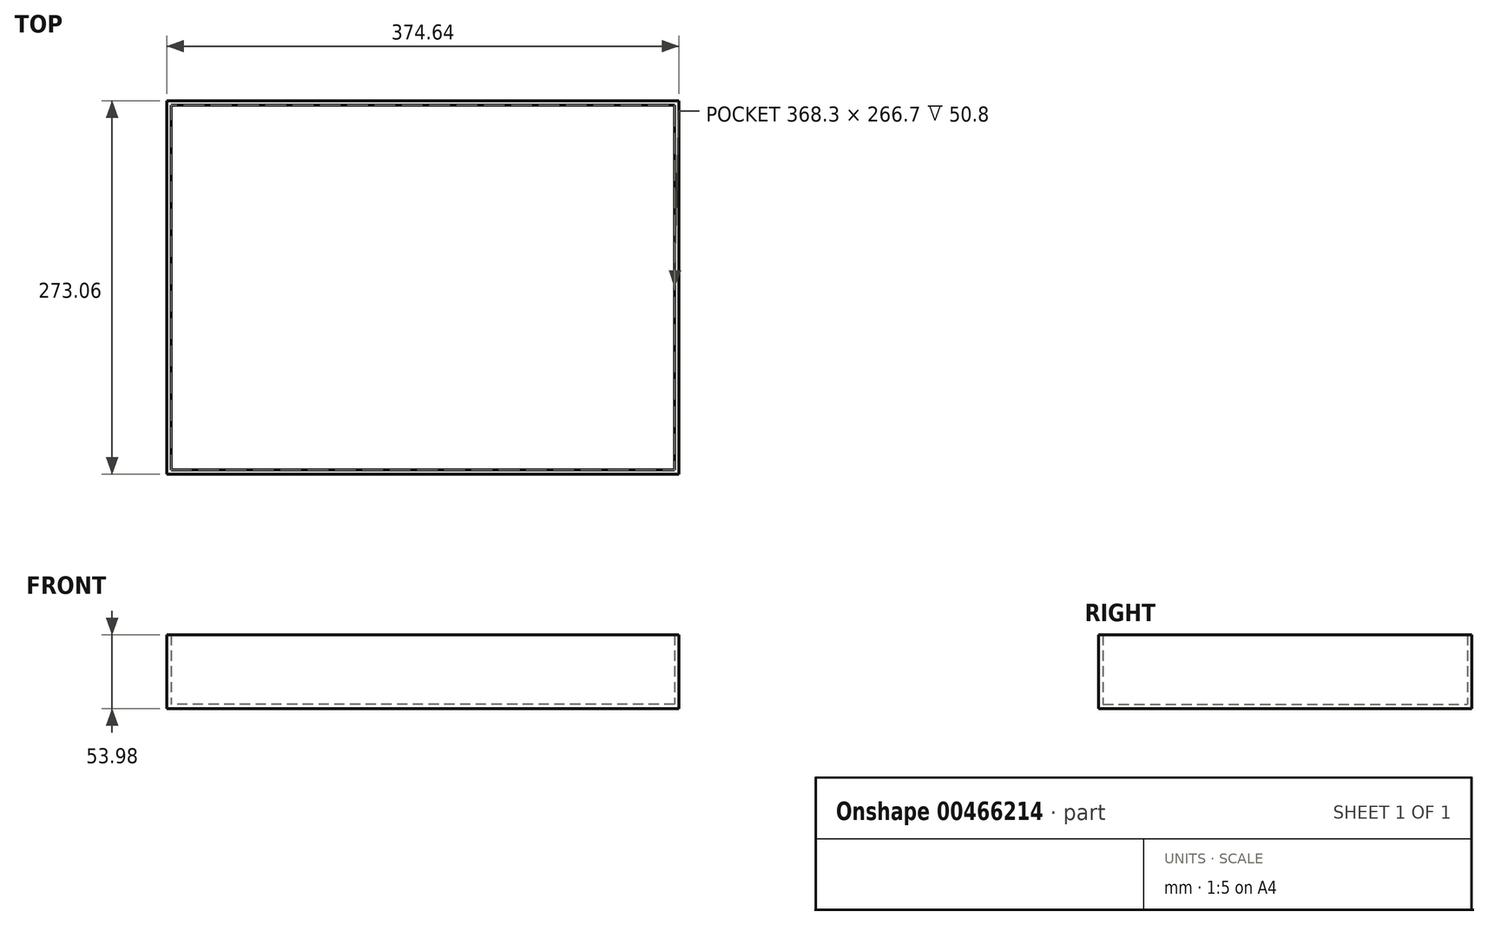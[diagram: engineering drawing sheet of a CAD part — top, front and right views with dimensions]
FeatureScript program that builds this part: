
annotation { "Feature Type Name" : "Feature", "Feature Type Description" : "" }
export const myFeature = defineFeature(function(context is Context, id is Id, definition is map)
    precondition{}
    {
        {
            var Q0;
            Q0=qCreatedBy(makeId("Top.planeOp"),FACE);
            var sketch = newSketch(context, id + "F0", { "sketchPlane" : qUnion([Q0])});
            skLineSegment(sketch, "E0.bottom", {"start": v(184.15, -133.35) * mm, "end": v(-184.15, -133.35) * mm});
            skLineSegment(sketch, "E0.top", {"start": v(184.15, 133.35) * mm, "end": v(-184.15, 133.35) * mm});
            skLineSegment(sketch, "E0.left", {"start": v(184.15, -133.35) * mm, "end": v(184.15, 133.35) * mm});
            skLineSegment(sketch, "E0.right", {"start": v(-184.15, -133.35) * mm, "end": v(-184.15, 133.35) * mm});
            skPoint(sketch, "E0.middle", {"position": v(0, 0) * mm});
            skLineSegment(sketch, "E1.0", {"start": v(187.32, 136.53) * mm, "end": v(-187.33, 136.53) * mm});
            skLineSegment(sketch, "E1.1", {"start": v(187.33, -136.53) * mm, "end": v(187.32, 136.53) * mm});
            skLineSegment(sketch, "E1.2", {"start": v(187.33, -136.53) * mm, "end": v(-187.32, -136.53) * mm});
            skLineSegment(sketch, "E1.3", {"start": v(-187.32, -136.53) * mm, "end": v(-187.33, 136.53) * mm});
            skSolve(sketch);
        }
        {
            var Q0;
            Q0=makeQuery(id+"F0.imprint","IMPRINT",FACE,{"disambiguationData":[TD([[makeQuery(id+"F0.imprint","IMPRINT",EDGE,{"derivedFrom":sQuery(id+"F0.wireOp",EDGE,"E0.bottom")}),1.0]])]});
            var Q1;
            Q1 = qConstructionFilter(qBodyType(qCreatedBy(id + "F0" ,EDGE), BodyType.WIRE), ConstructionObject.NO);
            extrude(context, id + "F1", {"entities" : qUnion([Q0]), "surfaceEntities" : qUnion([Q1]), "depth" : 53.97 * mm});
        }
        {
            var Q0;
            Q0=makeQuery(id+"F0.imprint","IMPRINT",FACE,{"disambiguationData":[TD([[makeQuery(id+"F0.imprint","IMPRINT",EDGE,{"derivedFrom":sQuery(id+"F0.wireOp",EDGE,"E0.bottom")}),-1.0]])]});
            extrude(context, id + "F2", {"entities" : qUnion([Q0]), "operationType" : NewBodyOperationType.ADD, "depth" : 3.17 * mm});
        }
    });
